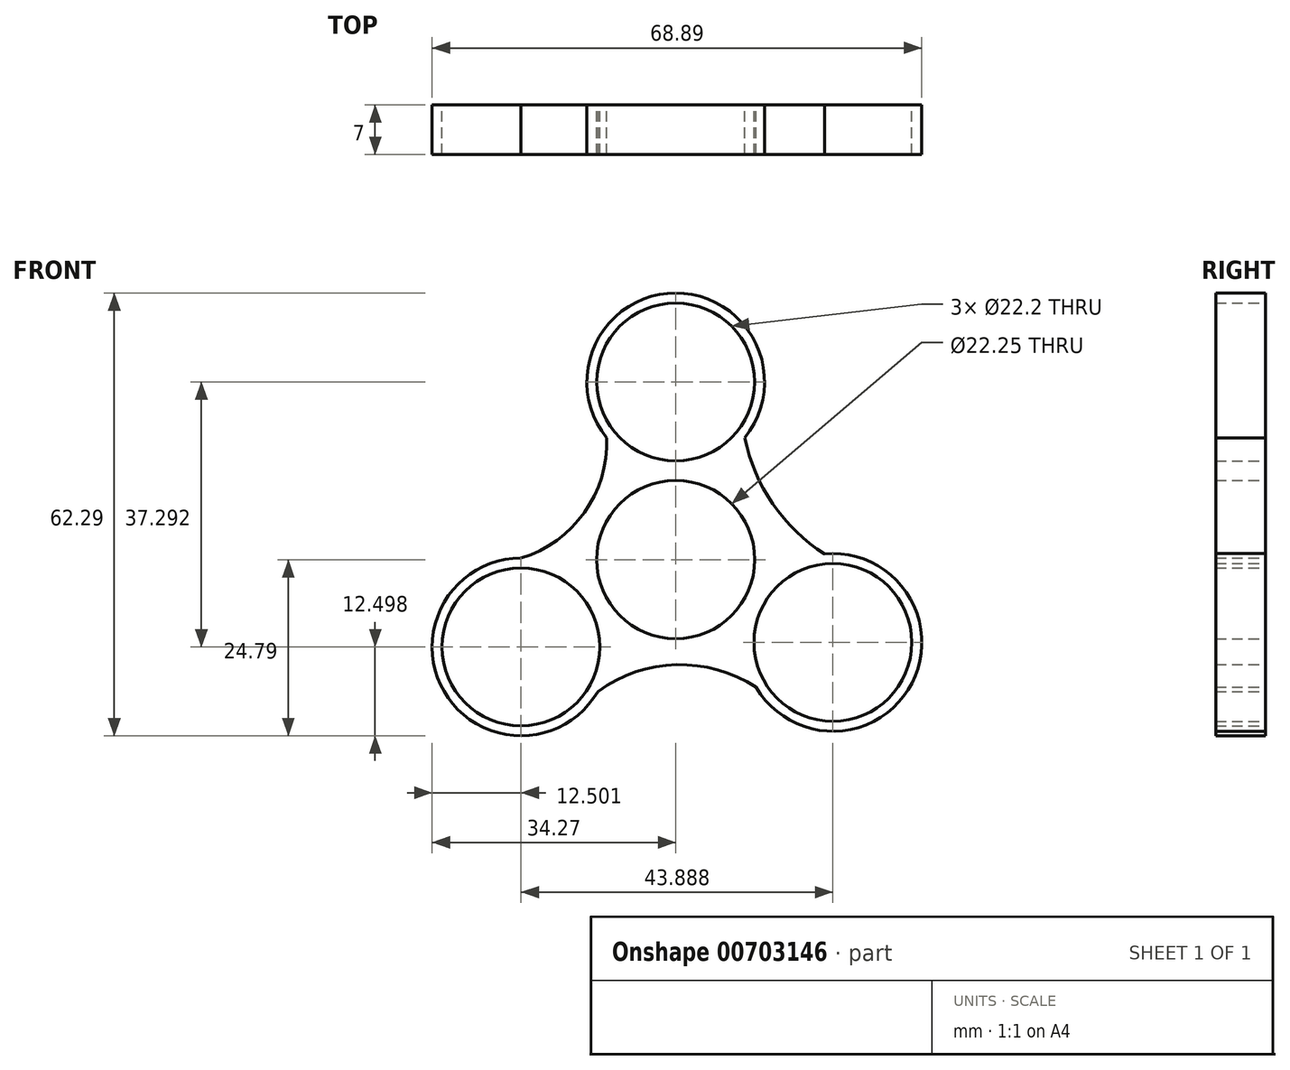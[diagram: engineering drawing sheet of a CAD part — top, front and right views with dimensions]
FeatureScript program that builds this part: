
annotation { "Feature Type Name" : "Feature", "Feature Type Description" : "" }
export const myFeature = defineFeature(function(context is Context, id is Id, definition is map)
    precondition{}
    {
        {
            var Q0;
            Q0=qCreatedBy(makeId("Front.planeOp"),FACE);
            var sketch = newSketch(context, id + "F0", { "sketchPlane" : qUnion([Q0])});
            skCircle(sketch, "E0", {"center": v(0, 0) * mm, "radius": 11.12 * mm});
            skArc(sketch, "E1", {"start": v(11.33, -17.96) * mm, "mid": v(33.24, -17.35) * mm, "end": v(20.95, 0.8) * mm});
            skArc(sketch, "E2", {"start": v(-21.77, 0.2) * mm, "mid": v(-32.6, -18.54) * mm, "end": v(-10.94, -18.54) * mm});
            skArc(sketch, "E3", {"start": v(9.72, 17.14) * mm, "mid": v(0, 37.5) * mm, "end": v(-9.72, 17.14) * mm});
            skPoint(sketch, "E4.orphan", {"position": v(0, -25.25) * mm});
            skCircle(sketch, "E5", {"center": v(0, 25) * mm, "radius": 11.1 * mm});
            skCircle(sketch, "E6", {"center": v(-21.77, -12.3) * mm, "radius": 11.1 * mm});
            skCircle(sketch, "E7", {"center": v(22.12, -11.65) * mm, "radius": 11.1 * mm});
            skArc(sketch, "E8", {"start": v(-21.77, 0.2) * mm, "mid": v(-12.86, 6.62) * mm, "end": v(-9.72, 17.14) * mm});
            skArc(sketch, "E9", {"start": v(9.72, 17.14) * mm, "mid": v(13.67, 7.83) * mm, "end": v(20.95, 0.8) * mm});
            skArc(sketch, "E10", {"start": v(11.33, -17.96) * mm, "mid": v(0.1, -14.8) * mm, "end": v(-10.94, -18.54) * mm});
            skSolve(sketch);
        }
        {
            var Q0;
            Q0=makeQuery(id+"F0.imprint","IMPRINT",FACE,{"disambiguationData":[TD([[makeQuery(id+"F0.imprint","IMPRINT",EDGE,{"derivedFrom":sQuery(id+"F0.wireOp",EDGE,"E0")}),-1.0]])]});
            extrude(context, id + "F1", {"entities" : qUnion([Q0]), "depth" : 7 * mm, "offsetDistance" : 25 * mm});
        }
    });
